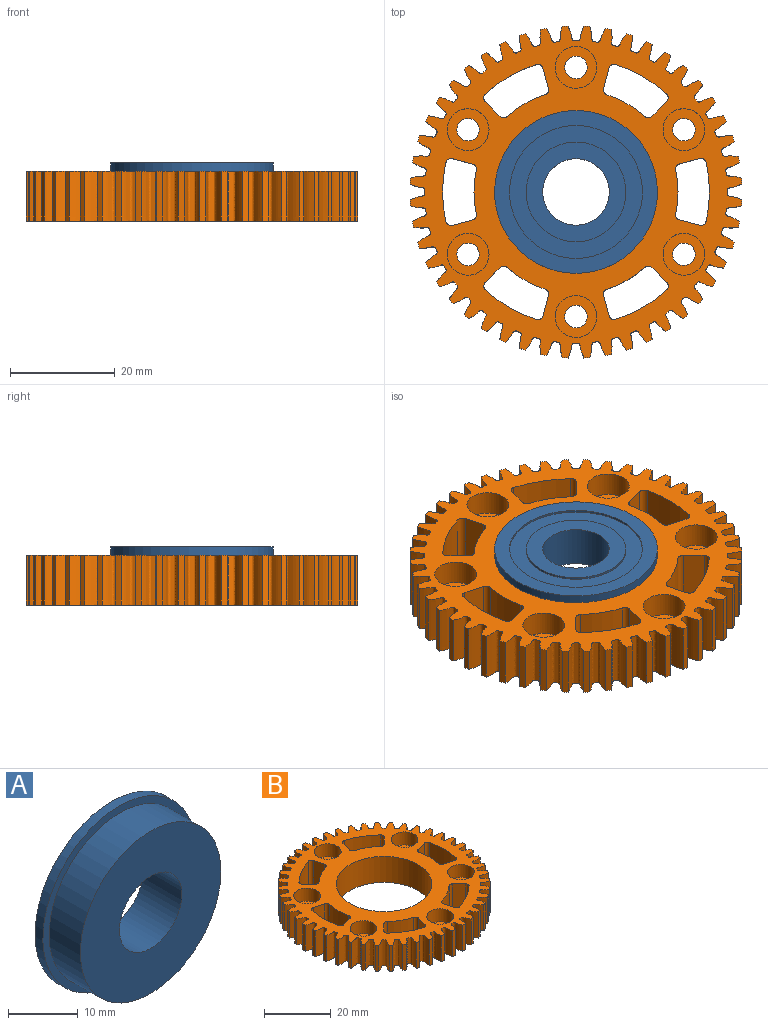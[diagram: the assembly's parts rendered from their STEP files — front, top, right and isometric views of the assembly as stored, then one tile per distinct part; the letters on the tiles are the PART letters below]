
ASSEMBLY  parts=2 mates=1
PART A: 10 faces, bbox 31.1x7.9x31.1 mm
  f0: cylinder r=12.7mm len=25.4mm, axis (0,1,0), area 30.4mm2, adj f8,f9
  f1: cylinder r=15.56mm len=31.12mm, axis (0,1,0), area 155.2mm2, adj f7,f8
  f2: cylinder r=14.29mm len=28.58mm, axis (0,1,0), area 570mm2, adj f6,f7
  f3: cylinder r=6.35mm len=12.7mm, axis (0,1,0), area 316.7mm2, adj f5,f6
  f4: cylinder r=9.53mm len=19.05mm, axis (0,1,0), area 22.8mm2, adj f5,f9
  f5: plane 19.05x19.05mm, normal (0,1,0), area 158.3mm2, adj f3,f4
  f6: plane 28.58x28.58mm, normal (0,-1,0), area 514.6mm2, adj f2,f3
  f7: plane 31.12x31.12mm, normal (0,-1,0), area 119.1mm2, adj f1,f2
  f8: plane 31.12x31.12mm, normal (0,1,0), area 253.7mm2, adj f0,f1
  f9: plane 25.4x25.4mm, normal (0,1,0), area 221.7mm2, adj f0,f4
PART B: 165 faces, bbox 63.4x63.4x9.5 mm
  f0: cylinder r=4mm len=8mm, axis (0,0,1), area 119.7mm2, adj f21,f164
  f1: cylinder r=4mm len=8mm, axis (0,0,1), area 119.7mm2, adj f21,f163
  f2: cylinder r=4mm len=8mm, axis (0,0,1), area 119.7mm2, adj f21,f162
  f3: cylinder r=4mm len=8mm, axis (0,0,1), area 119.7mm2, adj f21,f161
  f4: cylinder r=4mm len=8mm, axis (0,0,1), area 119.7mm2, adj f21,f160
  f5: cylinder r=4mm len=8mm, axis (0,0,1), area 119.7mm2, adj f21,f159
  f6: cylinder r=14.31mm len=28.61mm, axis (0,0,1), area 856.2mm2, adj f21,f22
  f7: cylinder r=1mm len=9.53mm, axis (0,0,1), area 15.3mm2, adj f21,f22,f152,f158
  f8: cylinder r=25.5mm len=11.26mm, axis (0,0,1), area 108.1mm2, adj f21,f22,f146,f151
  f9: cylinder r=19.5mm len=9.53mm, axis (0,0,1), area 79.8mm2, adj f21,f22,f148,f149
  f10: cylinder r=1mm len=9.53mm, axis (0,0,1), area 15.3mm2, adj f21,f22,f144,f145
  f11: cylinder r=1mm len=9.53mm, axis (0,0,1), area 14.5mm2, adj f21,f22,f135,f136
  f12: cylinder r=1mm len=9.53mm, axis (0,0,1), area 14.5mm2, adj f21,f22,f128,f129
  f13: cylinder r=1mm len=9.53mm, axis (0,0,1), area 14.5mm2, adj f21,f22,f127,f128
  f14: cylinder r=1mm len=9.53mm, axis (0,0,1), area 14.5mm2, adj f21,f22,f120,f121
  f15: cylinder r=2.15mm len=4.76mm, axis (0,0,1), area 64.3mm2, adj f22,f159
  f16: cylinder r=2.15mm len=4.76mm, axis (0,0,1), area 64.3mm2, adj f22,f160
  f17: cylinder r=2.15mm len=4.76mm, axis (0,0,1), area 64.3mm2, adj f22,f161
  f18: cylinder r=2.15mm len=4.76mm, axis (0,0,1), area 64.3mm2, adj f22,f162
  f19: cylinder r=2.15mm len=4.76mm, axis (0,0,1), area 64.3mm2, adj f22,f163
  f20: cylinder r=2.15mm len=4.76mm, axis (0,0,1), area 64.3mm2, adj f22,f164
  f21: plane 63.43x63.43mm, normal (0,0,1), area 1520.7mm2, adj f0,f1,f2,f3,f4,f5,f6,f7
  f22: plane 63.43x63.43mm, normal (0,0,-1), area 1735.2mm2, adj f6,f7,f8,f9,f10,f11,f12,f13
  f23: cylinder r=31.75mm len=9.53mm, axis (0,0,-1), area 10.8mm2, adj f21,f22,f117,f118
  f24: cylinder r=31.75mm len=9.53mm, axis (0,0,-1), area 10.8mm2, adj f21,f22,f116,f117
  f25: cylinder r=31.75mm len=9.53mm, axis (0,0,-1), area 10.8mm2, adj f21,f22,f115,f116
  f26: cylinder r=31.75mm len=9.53mm, axis (0,0,-1), area 10.8mm2, adj f21,f22,f114,f115
  f27: cylinder r=31.75mm len=9.53mm, axis (0,0,-1), area 10.8mm2, adj f21,f22,f113,f114
  f28: cylinder r=31.75mm len=9.53mm, axis (0,0,-1), area 10.8mm2, adj f21,f22,f112,f113
  f29: cylinder r=31.75mm len=9.53mm, axis (0,0,-1), area 10.8mm2, adj f21,f22,f111,f112
  f30: cylinder r=31.75mm len=9.53mm, axis (0,0,-1), area 10.8mm2, adj f21,f22,f110,f111
  f31: cylinder r=31.75mm len=9.53mm, axis (0,0,-1), area 10.8mm2, adj f21,f22,f109,f110
  f32: cylinder r=31.75mm len=9.53mm, axis (0,0,-1), area 10.8mm2, adj f21,f22,f108,f109
  f33: cylinder r=31.75mm len=9.53mm, axis (0,0,-1), area 10.8mm2, adj f21,f22,f107,f108
  f34: cylinder r=31.75mm len=9.53mm, axis (0,0,-1), area 10.8mm2, adj f21,f22,f106,f107
  f35: cylinder r=31.75mm len=9.53mm, axis (0,0,-1), area 10.8mm2, adj f21,f22,f105,f106
  f36: cylinder r=31.75mm len=9.53mm, axis (0,0,-1), area 10.8mm2, adj f21,f22,f104,f105
  f37: cylinder r=31.75mm len=9.53mm, axis (0,0,-1), area 10.8mm2, adj f21,f22,f103,f104
  f38: cylinder r=31.75mm len=9.53mm, axis (0,0,-1), area 10.8mm2, adj f21,f22,f102,f103
  f39: cylinder r=31.75mm len=9.53mm, axis (0,0,-1), area 10.8mm2, adj f21,f22,f101,f102
  f40: cylinder r=31.75mm len=9.53mm, axis (0,0,-1), area 10.8mm2, adj f21,f22,f100,f101
  f41: cylinder r=31.75mm len=9.53mm, axis (0,0,-1), area 10.8mm2, adj f21,f22,f99,f100
  f42: cylinder r=31.75mm len=9.53mm, axis (0,0,-1), area 10.8mm2, adj f21,f22,f98,f99
  f43: cylinder r=31.75mm len=9.53mm, axis (0,0,-1), area 10.8mm2, adj f21,f22,f97,f98
  f44: cylinder r=31.75mm len=9.53mm, axis (0,0,-1), area 10.8mm2, adj f21,f22,f96,f97
  f45: cylinder r=31.75mm len=9.53mm, axis (0,0,-1), area 10.8mm2, adj f21,f22,f95,f96
  f46: cylinder r=31.75mm len=9.53mm, axis (0,0,-1), area 10.8mm2, adj f21,f22,f94,f95
  f47: cylinder r=31.75mm len=9.53mm, axis (0,0,-1), area 10.8mm2, adj f21,f22,f93,f94
  f48: cylinder r=31.75mm len=9.53mm, axis (0,0,-1), area 10.8mm2, adj f21,f22,f92,f93
  f49: cylinder r=31.75mm len=9.53mm, axis (0,0,-1), area 10.8mm2, adj f21,f22,f91,f92
  f50: cylinder r=31.75mm len=9.53mm, axis (0,0,-1), area 10.8mm2, adj f21,f22,f90,f91
  f51: cylinder r=31.75mm len=9.53mm, axis (0,0,-1), area 10.8mm2, adj f21,f22,f89,f90
  f52: cylinder r=31.75mm len=9.53mm, axis (0,0,-1), area 10.8mm2, adj f21,f22,f88,f89
  f53: cylinder r=31.75mm len=9.53mm, axis (0,0,-1), area 10.8mm2, adj f21,f22,f87,f88
  f54: cylinder r=31.75mm len=9.53mm, axis (0,0,-1), area 10.8mm2, adj f21,f22,f86,f87
  f55: cylinder r=31.75mm len=9.53mm, axis (0,0,-1), area 10.8mm2, adj f21,f22,f85,f86
  f56: cylinder r=31.75mm len=9.53mm, axis (0,0,-1), area 10.8mm2, adj f21,f22,f84,f85
  f57: cylinder r=31.75mm len=9.53mm, axis (0,0,-1), area 10.8mm2, adj f21,f22,f83,f84
  f58: cylinder r=31.75mm len=9.53mm, axis (0,0,-1), area 10.8mm2, adj f21,f22,f82,f83
  f59: cylinder r=31.75mm len=9.53mm, axis (0,0,-1), area 10.8mm2, adj f21,f22,f81,f82
  f60: cylinder r=31.75mm len=9.53mm, axis (0,0,-1), area 10.8mm2, adj f21,f22,f80,f81
  f61: cylinder r=31.75mm len=9.53mm, axis (0,0,-1), area 10.8mm2, adj f21,f22,f79,f80
  f62: cylinder r=31.75mm len=9.53mm, axis (0,0,-1), area 10.8mm2, adj f21,f22,f78,f79
  f63: cylinder r=31.75mm len=9.53mm, axis (0,0,-1), area 10.8mm2, adj f21,f22,f77,f78
  f64: cylinder r=31.75mm len=9.53mm, axis (0,0,-1), area 10.8mm2, adj f21,f22,f76,f77
  f65: cylinder r=31.75mm len=9.53mm, axis (0,0,-1), area 10.8mm2, adj f21,f22,f75,f76
  f66: cylinder r=31.75mm len=9.53mm, axis (0,0,-1), area 10.8mm2, adj f21,f22,f74,f75
  f67: cylinder r=31.75mm len=9.53mm, axis (0,0,-1), area 10.8mm2, adj f21,f22,f73,f74
  f68: cylinder r=31.75mm len=9.53mm, axis (0,0,-1), area 10.8mm2, adj f21,f22,f72,f73
  f69: cylinder r=31.75mm len=9.53mm, axis (0,0,-1), area 10.8mm2, adj f21,f22,f71,f72
  f70: cylinder r=31.75mm len=9.53mm, axis (0,0,-1), area 10.8mm2, adj f21,f22,f71,f118
  f71: extruded ~9.53x3.02mm, area 66.8mm2, adj f21,f22,f69,f70
  f72: extruded ~9.53x3.02mm, area 66.8mm2, adj f21,f22,f68,f69
  f73: extruded ~9.53x3.2mm, area 66.8mm2, adj f21,f22,f67,f68
  f74: extruded ~9.53x3.33mm, area 66.8mm2, adj f21,f22,f66,f67
  f75: extruded ~9.53x3.39mm, area 66.8mm2, adj f21,f22,f65,f66
  f76: extruded ~9.53x3.43mm, area 66.8mm2, adj f21,f22,f64,f65
  f77: extruded ~9.53x3.41mm, area 66.8mm2, adj f21,f22,f63,f64
  f78: extruded ~9.53x3.43mm, area 66.8mm2, adj f21,f22,f62,f63
  f79: extruded ~9.53x3.39mm, area 66.8mm2, adj f21,f22,f61,f62
  f80: extruded ~9.53x3.33mm, area 66.8mm2, adj f21,f22,f60,f61
  f81: extruded ~9.53x3.2mm, area 66.8mm2, adj f21,f22,f59,f60
  f82: extruded ~9.53x3.02mm, area 66.8mm2, adj f21,f22,f58,f59
  f83: extruded ~9.53x3.02mm, area 66.8mm2, adj f21,f22,f57,f58
  f84: extruded ~9.53x3.02mm, area 66.8mm2, adj f21,f22,f56,f57
  f85: extruded ~9.53x3.2mm, area 66.8mm2, adj f21,f22,f55,f56
  f86: extruded ~9.53x3.33mm, area 66.8mm2, adj f21,f22,f54,f55
  f87: extruded ~9.53x3.39mm, area 66.8mm2, adj f21,f22,f53,f54
  f88: extruded ~9.53x3.43mm, area 66.8mm2, adj f21,f22,f52,f53
  f89: extruded ~9.53x3.41mm, area 66.8mm2, adj f21,f22,f51,f52
  f90: extruded ~9.53x3.43mm, area 66.8mm2, adj f21,f22,f50,f51
  f91: extruded ~9.53x3.39mm, area 66.8mm2, adj f21,f22,f49,f50
  f92: extruded ~9.53x3.33mm, area 66.8mm2, adj f21,f22,f48,f49
  f93: extruded ~9.53x3.2mm, area 66.8mm2, adj f21,f22,f47,f48
  f94: extruded ~9.53x3.02mm, area 66.8mm2, adj f21,f22,f46,f47
  f95: extruded ~9.53x3.02mm, area 66.8mm2, adj f21,f22,f45,f46
  f96: extruded ~9.53x3.02mm, area 66.8mm2, adj f21,f22,f44,f45
  f97: extruded ~9.53x3.2mm, area 66.8mm2, adj f21,f22,f43,f44
  f98: extruded ~9.53x3.33mm, area 66.8mm2, adj f21,f22,f42,f43
  f99: extruded ~9.53x3.39mm, area 66.8mm2, adj f21,f22,f41,f42
  f100: extruded ~9.53x3.43mm, area 66.8mm2, adj f21,f22,f40,f41
  f101: extruded ~9.53x3.41mm, area 66.8mm2, adj f21,f22,f39,f40
  f102: extruded ~9.53x3.43mm, area 66.8mm2, adj f21,f22,f38,f39
  f103: extruded ~9.53x3.39mm, area 66.8mm2, adj f21,f22,f37,f38
  f104: extruded ~9.53x3.33mm, area 66.8mm2, adj f21,f22,f36,f37
  f105: extruded ~9.53x3.2mm, area 66.8mm2, adj f21,f22,f35,f36
  f106: extruded ~9.53x3.02mm, area 66.8mm2, adj f21,f22,f34,f35
  f107: extruded ~9.53x3.02mm, area 66.8mm2, adj f21,f22,f33,f34
  f108: extruded ~9.53x3.02mm, area 66.8mm2, adj f21,f22,f32,f33
  f109: extruded ~9.53x3.2mm, area 66.8mm2, adj f21,f22,f31,f32
  f110: extruded ~9.53x3.33mm, area 66.8mm2, adj f21,f22,f30,f31
  f111: extruded ~9.53x3.39mm, area 66.8mm2, adj f21,f22,f29,f30
  f112: extruded ~9.53x3.43mm, area 66.8mm2, adj f21,f22,f28,f29
  f113: extruded ~9.53x3.41mm, area 66.8mm2, adj f21,f22,f27,f28
  f114: extruded ~9.53x3.43mm, area 66.8mm2, adj f21,f22,f26,f27
  f115: extruded ~9.53x3.39mm, area 66.8mm2, adj f21,f22,f25,f26
  f116: extruded ~9.53x3.33mm, area 66.8mm2, adj f21,f22,f24,f25
  f117: extruded ~9.53x3.2mm, area 66.8mm2, adj f21,f22,f23,f24
  f118: extruded ~9.53x3.02mm, area 66.8mm2, adj f21,f22,f23,f70
  f119: cylinder r=1mm len=9.53mm, axis (0,0,1), area 15.3mm2, adj f21,f22,f120,f125
  f120: plane 9.53x3.87mm, normal (-0.97,-0.26,0), area 38.1mm2, adj f14,f21,f22,f119
  f121: cylinder r=19.5mm len=9.53mm, axis (0,0,1), area 79.8mm2, adj f14,f21,f22,f122
  f122: cylinder r=1mm len=9.53mm, axis (0,0,1), area 14.5mm2, adj f21,f22,f121,f123
  f123: plane 9.53x2.83mm, normal (0.71,0.71,0), area 38.1mm2, adj f21,f22,f122,f124
  f124: cylinder r=1mm len=9.53mm, axis (0,0,1), area 15.3mm2, adj f21,f22,f123,f125
  f125: cylinder r=25.5mm len=9.74mm, axis (0,0,1), area 108.1mm2, adj f21,f22,f119,f124
  f126: cylinder r=1mm len=9.53mm, axis (0,0,1), area 15.3mm2, adj f21,f22,f127,f131
  f127: plane 9.53x3.87mm, normal (-0.26,-0.97,0), area 38.1mm2, adj f13,f21,f22,f126
  f128: cylinder r=19.5mm len=9.53mm, axis (0,0,1), area 79.8mm2, adj f12,f13,f21,f22
  f129: plane 9.53x3.87mm, normal (-0.26,0.97,0), area 38.1mm2, adj f12,f21,f22,f130
  f130: cylinder r=1mm len=9.53mm, axis (0,0,1), area 15.3mm2, adj f21,f22,f129,f131
  f131: cylinder r=25.5mm len=11.26mm, axis (0,0,1), area 108.1mm2, adj f21,f22,f126,f130
  f132: cylinder r=1mm len=9.53mm, axis (0,0,1), area 15.3mm2, adj f21,f22,f133,f138
  f133: plane 9.53x2.83mm, normal (0.71,-0.71,0), area 38.1mm2, adj f21,f22,f132,f134
  f134: cylinder r=1mm len=9.53mm, axis (0,0,1), area 14.5mm2, adj f21,f22,f133,f135
  f135: cylinder r=19.5mm len=9.53mm, axis (0,0,1), area 79.8mm2, adj f11,f21,f22,f134
  f136: plane 9.53x3.87mm, normal (-0.97,0.26,0), area 38.1mm2, adj f11,f21,f22,f137
  f137: cylinder r=1mm len=9.53mm, axis (0,0,1), area 15.3mm2, adj f21,f22,f136,f138
  f138: cylinder r=25.5mm len=9.75mm, axis (0,0,1), area 108.1mm2, adj f21,f22,f132,f137
  f139: cylinder r=1mm len=9.53mm, axis (0,0,1), area 15.3mm2, adj f21,f22,f140,f145
  f140: plane 9.53x3.87mm, normal (0.97,0.26,0), area 38.1mm2, adj f21,f22,f139,f141
  f141: cylinder r=1mm len=9.53mm, axis (0,0,1), area 14.5mm2, adj f21,f22,f140,f142
  f142: cylinder r=19.5mm len=9.53mm, axis (0,0,1), area 79.8mm2, adj f21,f22,f141,f143
  f143: cylinder r=1mm len=9.53mm, axis (0,0,1), area 14.5mm2, adj f21,f22,f142,f144
  f144: plane 9.53x2.83mm, normal (-0.71,-0.71,0), area 38.1mm2, adj f10,f21,f22,f143
  f145: cylinder r=25.5mm len=9.74mm, axis (0,0,1), area 108.1mm2, adj f10,f21,f22,f139
  f146: cylinder r=1mm len=9.53mm, axis (0,0,1), area 15.3mm2, adj f8,f21,f22,f147
  f147: plane 9.53x3.87mm, normal (0.26,0.97,0), area 38.1mm2, adj f21,f22,f146,f148
  f148: cylinder r=1mm len=9.53mm, axis (0,0,1), area 14.5mm2, adj f9,f21,f22,f147
  f149: cylinder r=1mm len=9.53mm, axis (0,0,1), area 14.5mm2, adj f9,f21,f22,f150
  f150: plane 9.53x3.87mm, normal (0.26,-0.97,0), area 38.1mm2, adj f21,f22,f149,f151
  f151: cylinder r=1mm len=9.53mm, axis (0,0,1), area 15.3mm2, adj f8,f21,f22,f150
  f152: plane 9.53x2.83mm, normal (-0.71,0.71,0), area 38.1mm2, adj f7,f21,f22,f153
  f153: cylinder r=1mm len=9.53mm, axis (0,0,1), area 14.5mm2, adj f21,f22,f152,f154
  f154: cylinder r=19.5mm len=9.53mm, axis (0,0,1), area 79.8mm2, adj f21,f22,f153,f155
  f155: cylinder r=1mm len=9.53mm, axis (0,0,1), area 14.5mm2, adj f21,f22,f154,f156
  f156: plane 9.53x3.87mm, normal (0.97,-0.26,0), area 38.1mm2, adj f21,f22,f155,f157
  f157: cylinder r=1mm len=9.53mm, axis (0,0,1), area 15.3mm2, adj f21,f22,f156,f158
  f158: cylinder r=25.5mm len=9.75mm, axis (0,0,1), area 108.1mm2, adj f7,f21,f22,f157
  f159: plane 8x8mm, normal (0,0,1), area 35.7mm2, adj f5,f15
  f160: plane 8x8mm, normal (0,0,1), area 35.7mm2, adj f4,f16
  f161: plane 8x8mm, normal (0,0,1), area 35.7mm2, adj f3,f17
  f162: plane 8x8mm, normal (0,0,1), area 35.7mm2, adj f2,f18
  f163: plane 8x8mm, normal (0,0,1), area 35.7mm2, adj f1,f19
  f164: plane 8x8mm, normal (0,0,1), area 35.7mm2, adj f0,f20
PLACE A rot(axis=(1,0,0),90deg) t=(-0.17,0.15,-2.13)mm
PLACE B t=(-0.17,0.15,-0.54)mm
MATE fastened B.f6 <-> A.f0  axis (0,0,1) through (-0.17,0.15,4.22)mm
